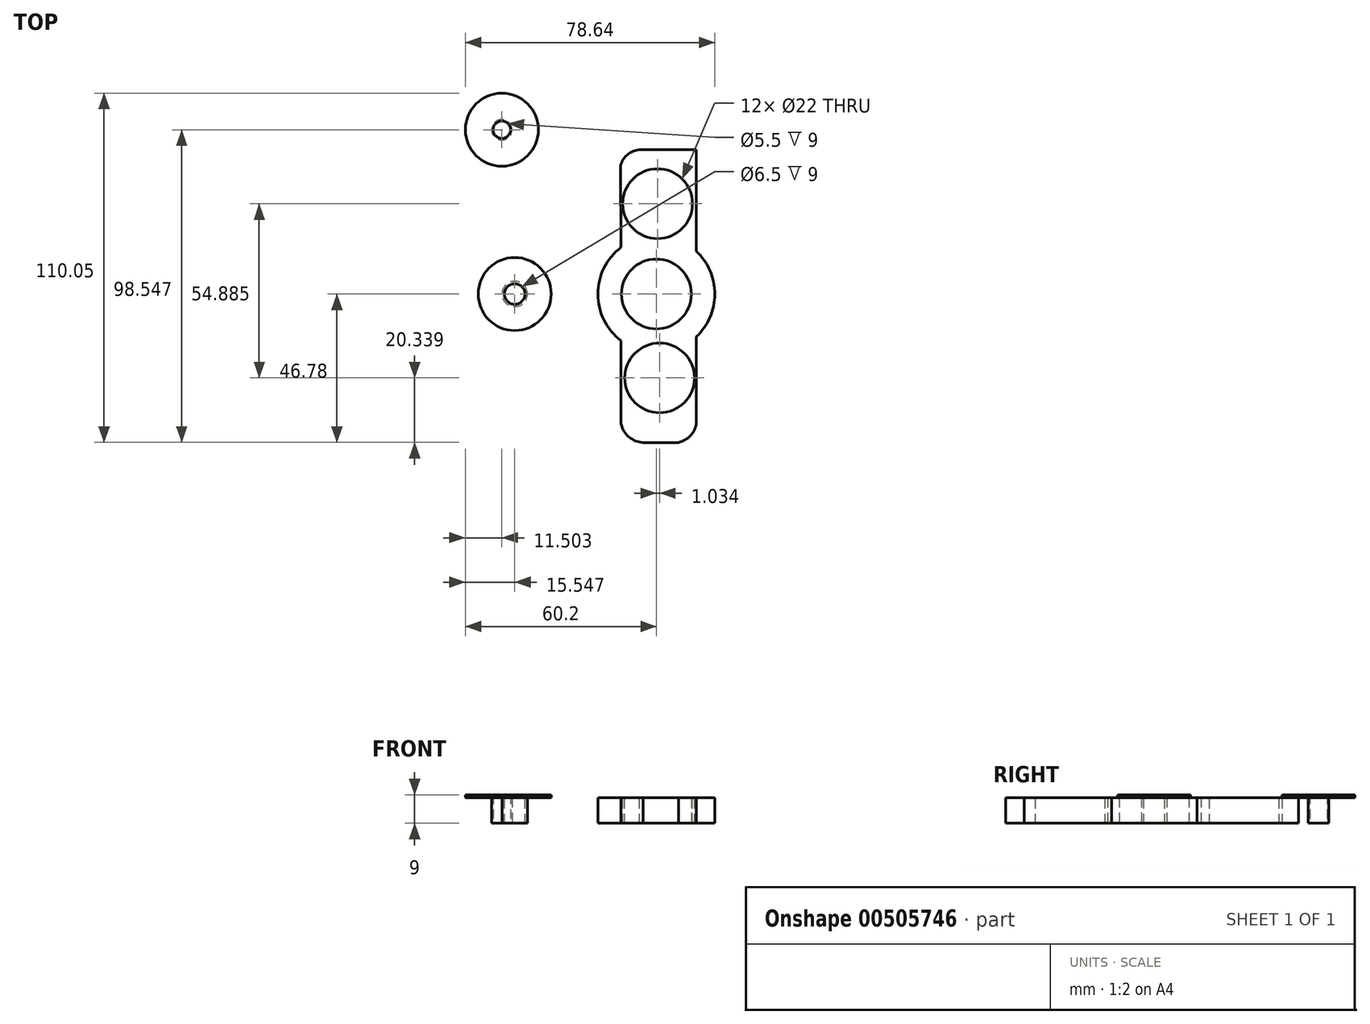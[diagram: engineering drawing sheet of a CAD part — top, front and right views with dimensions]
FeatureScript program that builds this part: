
annotation { "Feature Type Name" : "Feature", "Feature Type Description" : "" }
export const myFeature = defineFeature(function(context is Context, id is Id, definition is map)
    precondition{}
    {
        {
            var Q0;
            Q0=qCreatedBy(makeId("Top.planeOp"),FACE);
            var sketch = newSketch(context, id + "F0", { "sketchPlane" : qUnion([Q0])});
            skCircle(sketch, "E0", {"center": v(0, 0) * mm, "radius": 11 * mm});
            skCircle(sketch, "E1", {"center": v(0, 0) * mm, "radius": 18.44 * mm});
            skLineSegment(sketch, "E2", {"start": v(-11.12, 14.72) * mm, "end": v(-11.36, 45.43) * mm});
            skLineSegment(sketch, "E3", {"start": v(-11.36, 45.43) * mm, "end": v(12.64, 45.43) * mm});
            skLineSegment(sketch, "E4", {"start": v(12.64, 45.43) * mm, "end": v(12.64, 13.43) * mm});
            skLineSegment(sketch, "E5", {"start": v(-11.12, -14.72) * mm, "end": v(-11.12, -46.78) * mm});
            skLineSegment(sketch, "E6", {"start": v(12.64, -13.43) * mm, "end": v(12.64, -46.78) * mm});
            skLineSegment(sketch, "E7", {"start": v(12.64, -46.78) * mm, "end": v(-11.12, -46.78) * mm});
            skSolve(sketch);
        }
        {
            var Q0;
            {var subQ0=sQuery(id+"F0.wireOp",EDGE,"E2");Q0=makeQuery(id+"F0.imprint","IMPRINT",FACE,{"disambiguationData":[TD([[makeQuery(id+"F0.imprint","IMPRINT",EDGE,{"derivedFrom":subQ0}),-1.0]])]});}
            var Q1;
            Q1=makeQuery(id+"F0.imprint","IMPRINT",FACE,{"disambiguationData":[TD([[makeQuery(id+"F0.imprint","IMPRINT",EDGE,{"derivedFrom":sQuery(id+"F0.wireOp",EDGE,"E0")}),-1.0]])]});
            var Q2;
            {var subQ0=sQuery(id+"F0.wireOp",EDGE,"E5");Q2=makeQuery(id+"F0.imprint","IMPRINT",FACE,{"disambiguationData":[TD([[makeQuery(id+"F0.imprint","IMPRINT",EDGE,{"derivedFrom":subQ0}),1.0]])]});}
            extrude(context, id + "F1", {"entities" : qUnion([Q0, Q1, Q2]), "depth" : 8 * mm});
        }
        {
            var Q0;
            Q0=makeQuery(id+"F1.opExtrude","CAP_FACE",FACE,{"disambiguationData":[OSD([sQuery(id+"F0.wireOp",EDGE,"E0"),sQuery(id+"F0.wireOp",EDGE,"E1"),sQuery(id+"F0.wireOp",EDGE,"E2"),sQuery(id+"F0.wireOp",EDGE,"E3"),sQuery(id+"F0.wireOp",EDGE,"E4"),sQuery(id+"F0.wireOp",EDGE,"E5"),sQuery(id+"F0.wireOp",EDGE,"E6"),sQuery(id+"F0.wireOp",EDGE,"E7")])],"isStart":false});
            var sketch = newSketch(context, id + "F2", { "sketchPlane" : qUnion([Q0])});
            skArc(sketch, "E8", {"start": v(-11.12, -37.97) * mm, "mid": v(-9.67, -44) * mm, "end": v(-4.13, -46.78) * mm});
            skArc(sketch, "E9", {"start": v(6.95, -46.78) * mm, "mid": v(11.59, -43.53) * mm, "end": v(12.64, -37.97) * mm});
            skArc(sketch, "E10", {"start": v(12.64, 37.03) * mm, "mid": v(11.6, 43.27) * mm, "end": v(5.64, 45.43) * mm});
            skArc(sketch, "E11", {"start": v(-4.13, 45.43) * mm, "mid": v(-9.92, 43.1) * mm, "end": v(-11.36, 37.03) * mm});
            skSolve(sketch);
        }
        {
            var Q0;
            {var subQ0=sQuery(id+"F2.wireOp",EDGE,"E11");var subQ1=makeQuery(id+"F1.opExtrude","CAP_EDGE",EDGE,{"disambiguationData":[OSD([sQuery(id+"F0.wireOp",EDGE,"E2")])],"isStart":false});var subQ2=makeQuery(id+"F2.imprint","INTERSECT",VERTEX,{"derivedFrom":[subQ1,subQ0]});Q0=makeQuery(id+"F2.imprint","IMPRINT",FACE,{"disambiguationData":[TD([[makeQuery(id+"F2.imprint","IMPRINT",EDGE,{"disambiguationData":[TD([[subQ2,1.0]])],"derivedFrom":subQ0}),-1.0]])]});}
            var Q1;
            {var subQ0=sQuery(id+"F2.wireOp",EDGE,"E10");var subQ1=makeQuery(id+"F1.opExtrude","CAP_EDGE",EDGE,{"disambiguationData":[OSD([sQuery(id+"F0.wireOp",EDGE,"E4")])],"isStart":false});var subQ2=makeQuery(id+"F2.imprint","INTERSECT",VERTEX,{"disambiguationData":[OD(1.0)],"derivedFrom":[subQ1,subQ0]});Q1=makeQuery(id+"F2.imprint","IMPRINT",FACE,{"disambiguationData":[TD([[makeQuery(id+"F2.imprint","IMPRINT",EDGE,{"disambiguationData":[TD([[subQ2,-1.0]])],"derivedFrom":subQ0}),-1.0]])]});}
            var Q2;
            {var subQ0=sQuery(id+"F2.wireOp",EDGE,"E8");var subQ1=makeQuery(id+"F1.opExtrude","CAP_EDGE",EDGE,{"disambiguationData":[OSD([sQuery(id+"F0.wireOp",EDGE,"E7")])],"isStart":false});var subQ2=makeQuery(id+"F2.imprint","INTERSECT",VERTEX,{"derivedFrom":[subQ1,subQ0]});Q2=makeQuery(id+"F2.imprint","IMPRINT",FACE,{"disambiguationData":[TD([[makeQuery(id+"F2.imprint","IMPRINT",EDGE,{"disambiguationData":[TD([[subQ2,1.0]])],"derivedFrom":subQ0}),-1.0]])]});}
            var Q3;
            {var subQ0=sQuery(id+"F2.wireOp",EDGE,"E9");var subQ1=makeQuery(id+"F1.opExtrude","CAP_EDGE",EDGE,{"disambiguationData":[OSD([sQuery(id+"F0.wireOp",EDGE,"E7")])],"isStart":false});var subQ2=makeQuery(id+"F2.imprint","INTERSECT",VERTEX,{"derivedFrom":[subQ1,subQ0]});Q3=makeQuery(id+"F2.imprint","IMPRINT",FACE,{"disambiguationData":[TD([[makeQuery(id+"F2.imprint","IMPRINT",EDGE,{"disambiguationData":[TD([[subQ2,-1.0]])],"derivedFrom":subQ0}),-1.0]])]});}
            extrude(context, id + "F3", {"entities" : qUnion([Q0, Q1, Q2, Q3]), "operationType" : NewBodyOperationType.REMOVE, "oppositeDirection" : true, "depth" : 25 * mm});
        }
        {
            var Q0;
            Q0=qCreatedBy(makeId("Top.planeOp"),FACE);
            var sketch = newSketch(context, id + "F4", { "sketchPlane" : qUnion([Q0])});
            skCircle(sketch, "E12", {"center": v(-44.65, 0) * mm, "radius": 4 * mm});
            skSolve(sketch);
        }
        {
            var Q0;
            Q0=makeQuery(id+"F4.imprint","IMPRINT",FACE,{"disambiguationData":[TD([[makeQuery(id+"F4.imprint","IMPRINT",EDGE,{"derivedFrom":sQuery(id+"F4.wireOp",EDGE,"E12")}),1.0]])]});
            extrude(context, id + "F5", {"entities" : qUnion([Q0]), "depth" : 8 * mm});
        }
        {
            var Q0;
            Q0=makeQuery(id+"F5.opExtrude","CAP_FACE",FACE,{"disambiguationData":[OSD([sQuery(id+"F4.wireOp",EDGE,"E12")])],"isStart":false});
            var sketch = newSketch(context, id + "F6", { "sketchPlane" : qUnion([Q0])});
            skCircle(sketch, "E13", {"center": v(-44.65, 0) * mm, "radius": 3.25 * mm});
            skSolve(sketch);
        }
        {
            var Q0;
            Q0=makeQuery(id+"F6.imprint","IMPRINT",FACE,{"disambiguationData":[TD([[makeQuery(id+"F6.imprint","IMPRINT",EDGE,{"derivedFrom":sQuery(id+"F6.wireOp",EDGE,"E13")}),1.0]])]});
            extrude(context, id + "F7", {"entities" : qUnion([Q0]), "operationType" : NewBodyOperationType.REMOVE, "oppositeDirection" : true, "depth" : 25 * mm});
        }
        {
            var Q0;
            Q0=makeQuery(id+"F5.opExtrude","CAP_FACE",FACE,{"disambiguationData":[OSD([sQuery(id+"F4.wireOp",EDGE,"E12")])],"isStart":false});
            var sketch = newSketch(context, id + "F8", { "sketchPlane" : qUnion([Q0])});
            skCircle(sketch, "E14", {"center": v(-44.65, 0) * mm, "radius": 11.5 * mm});
            skSolve(sketch);
        }
        {
            var Q0;
            Q0 = qSketchRegion(id + "F8", true);
            extrude(context, id + "F9", {"entities" : qUnion([Q0]), "operationType" : NewBodyOperationType.ADD, "depth" : 1 * mm});
        }
        {
            var Q0;
            Q0=makeQuery(id+"F9.boolean.opBoolean","SPLIT",FACE,{"disambiguationData":[TD([makeQuery(id+"F7.boolean.opBoolean","COPY",FACE,{"derivedFrom":makeQuery(id+"F7.opExtrude","SWEPT_FACE",FACE,{"disambiguationData":[OSD([sQuery(id+"F6.wireOp",EDGE,"E13")])]})})])],"derivedFrom":makeQuery(id+"F9.opExtrude","CAP_FACE",FACE,{"disambiguationData":[OSD([sQuery(id+"F8.wireOp",EDGE,"E14")])],"isStart":true})});
            var sketch = newSketch(context, id + "F10", { "sketchPlane" : qUnion([Q0])});
            skCircle(sketch, "E15", {"center": v(-44.65, 0) * mm, "radius": 3.25 * mm});
            skSolve(sketch);
        }
        {
            var Q0;
            Q0 = qSketchRegion(id + "F10", true);
            extrude(context, id + "F11", {"entities" : qUnion([Q0]), "operationType" : NewBodyOperationType.REMOVE, "oppositeDirection" : true, "depth" : 25 * mm});
        }
        {
            var Q0;
            Q0=qCreatedBy(makeId("Top.planeOp"),FACE);
            var sketch = newSketch(context, id + "F12", { "sketchPlane" : qUnion([Q0])});
            skCircle(sketch, "E16", {"center": v(-48.7, 51.77) * mm, "radius": 3.2 * mm});
            skSolve(sketch);
        }
        {
            var Q0;
            Q0=makeQuery(id+"F12.imprint","IMPRINT",FACE,{"disambiguationData":[TD([[makeQuery(id+"F12.imprint","IMPRINT",EDGE,{"derivedFrom":sQuery(id+"F12.wireOp",EDGE,"E16")}),1.0]])]});
            extrude(context, id + "F13", {"entities" : qUnion([Q0]), "depth" : 8 * mm});
        }
        {
            var Q0;
            Q0=makeQuery(id+"F13.opExtrude","CAP_FACE",FACE,{"disambiguationData":[OSD([sQuery(id+"F12.wireOp",EDGE,"E16")])],"isStart":false});
            var sketch = newSketch(context, id + "F14", { "sketchPlane" : qUnion([Q0])});
            skCircle(sketch, "E17", {"center": v(-48.7, 51.77) * mm, "radius": 11.5 * mm});
            skSolve(sketch);
        }
        {
            var Q0;
            Q0 = qSketchRegion(id + "F14", true);
            var Q1;
            Q1=makeQuery(id+"F14.imprint","IMPRINT",FACE,{"disambiguationData":[TD([[makeQuery(id+"F14.imprint","IMPRINT",EDGE,{"derivedFrom":makeQuery(id+"F13.opExtrude","CAP_EDGE",EDGE,{"disambiguationData":[OSD([sQuery(id+"F12.wireOp",EDGE,"E16")])],"isStart":false})}),1.0]])]});
            extrude(context, id + "F15", {"entities" : qUnion([Q0, Q1]), "operationType" : NewBodyOperationType.ADD, "depth" : 1 * mm});
        }
        {
            var Q0;
            Q0=makeQuery(id+"F13.opExtrude","CAP_FACE",FACE,{"disambiguationData":[OSD([sQuery(id+"F12.wireOp",EDGE,"E16")])],"isStart":true});
            var sketch = newSketch(context, id + "F16", { "sketchPlane" : qUnion([Q0])});
            skCircle(sketch, "E18", {"center": v(-48.7, -51.77) * mm, "radius": 2.75 * mm});
            skSolve(sketch);
        }
        {
            var Q0;
            Q0=makeQuery(id+"F16.imprint","IMPRINT",FACE,{"disambiguationData":[TD([[makeQuery(id+"F16.imprint","IMPRINT",EDGE,{"derivedFrom":sQuery(id+"F16.wireOp",EDGE,"E18")}),1.0]])]});
            extrude(context, id + "F17", {"entities" : qUnion([Q0]), "operationType" : NewBodyOperationType.REMOVE, "oppositeDirection" : true, "depth" : 25 * mm});
        }
        {
            var Q0;
            Q0=makeQuery(id+"F1.opExtrude","CAP_FACE",FACE,{"disambiguationData":[OSD([sQuery(id+"F0.wireOp",EDGE,"E0"),sQuery(id+"F0.wireOp",EDGE,"E1"),sQuery(id+"F0.wireOp",EDGE,"E2"),sQuery(id+"F0.wireOp",EDGE,"E3"),sQuery(id+"F0.wireOp",EDGE,"E4"),sQuery(id+"F0.wireOp",EDGE,"E5"),sQuery(id+"F0.wireOp",EDGE,"E6"),sQuery(id+"F0.wireOp",EDGE,"E7")])],"isStart":false});
            var sketch = newSketch(context, id + "F18", { "sketchPlane" : qUnion([Q0])});
            skCircle(sketch, "E19", {"center": v(1.03, -26.44) * mm, "radius": 11 * mm});
            skCircle(sketch, "E20", {"center": v(0.38, 28.44) * mm, "radius": 11 * mm});
            skSolve(sketch);
        }
        {
            var Q0;
            Q0 = qSketchRegion(id + "F18", true);
            extrude(context, id + "F19", {"entities" : qUnion([Q0]), "operationType" : NewBodyOperationType.REMOVE, "oppositeDirection" : true, "depth" : 25 * mm});
        }
    });
